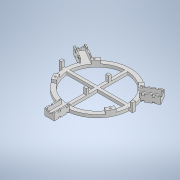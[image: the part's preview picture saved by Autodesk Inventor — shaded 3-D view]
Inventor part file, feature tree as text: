
AUTODESK INVENTOR PART (.ipt)
format: ipt  version: 2020.2 (Build 242310000, 310)  size: 588,288 bytes
history: native  units: mm
features: sketch x9, extrude x8, projected_geometry x7, plane x2, pattern_circular x1, hole x1
ambient origin geometry x8: Origin, YZ Plane, XZ Plane, XY Plane, X Axis, Y Axis, Z Axis, Center Point
bodies: Solid1 (feature_tree)
feature tree (28):
  extrude  "Extrusion1"  Depth=100.0mm
  extrude  "Extrusion7"  Depth=5.0mm TaperAngle=0.0deg
  extrude  "Extrusion8"  Depth=2.0mm
  extrude  "Extrusion5"  Depth=5.0mm
  extrude  "Extrusion6"  Depth=2.0mm
  plane  "Work Plane1"
  plane  "Work Plane2"
  extrude  "Extrusion12"  Depth=13.5mm TaperAngle=0.0deg
  extrude  "Extrusion13"  Depth=3.0mm
  pattern_circular  "Circular Pattern3"  [2 undecoded]
  extrude  "Extrusion9"  Depth=0.5mm
  hole  "Hole1"  [1 undecoded]
  sketch  "Sketch1"  dims[d0=114.0mm d1=100.0mm]
  sketch  "Sketch6"  dims[d10=16.0mm d20=5.0mm d21=0.0mm]
  sketch  "Sketch7"  dims[d46=27.0mm d47=2.0mm]
  sketch  "Sketch8"  dims[d48=7.0mm d49=0.0mm d51=5.0mm]
  sketch  "Sketch9"  dims[d53=9.0mm d54=2.0mm]
  sketch  "Sketch10"  dims[d55=2.0mm d56=13.5mm d57=0.0mm]
  projected_geometry  "Projected Loop1"
  sketch  "Sketch11"  dims[d61=107.0mm d62=3.0mm]
  projected_geometry  "Projected Loop2"
  sketch  "Sketch14"  dims[d63=3.0mm]
  projected_geometry  "Projected Loop5"
  sketch  "Sketch15"  dims[d64=3.0mm d65=3.0mm d66=35.0mm d67=35.0mm d68=25.0mm d69=25.0mm d71=32.0mm d90=30.0mm d92=360.0deg d94=5.0mm d95=30.0mm d96=360.0deg d98=118.0mm d99=34.0mm d100=5.0mm d101=4.2mm d102=5.0mm d103=5.0mm d104=0.0mm d105=118.0mm d106=34.0mm d107=4.0mm d108=4.0mm d109=0.2mm d110=10.0mm d111=0.0mm d112=0.2mm d113=13.0mm d114=8.0mm d115=8.0mm d116=13.0mm d117=5.0mm d118=0.0mm d119=6.0mm d120=6.0mm d121=18.0mm d122=4.8mm d123=90.0deg d124=5.0mm d125=20.594885mm d136=7.0mm d137=22.0mm d138=3.0mm d139=3.6mm d140=0.0mm d141=3.6mm d142=0.0mm d143=2.0mm d144=45.0deg d126=0.5mm d127=0.872665mm d128=0.5mm d129=0.872665mm]
  projected_geometry  "Projected Loop6"
  projected_geometry  "Projected Loop7"
  projected_geometry  "Projected Loop8"
  projected_geometry  "Projected Loop9"
note: 3 required parameter values undecoded (feature->parameter linkage not recoverable at this tier; creation-order binding heuristic only, values carry confidence <= 0.55)
